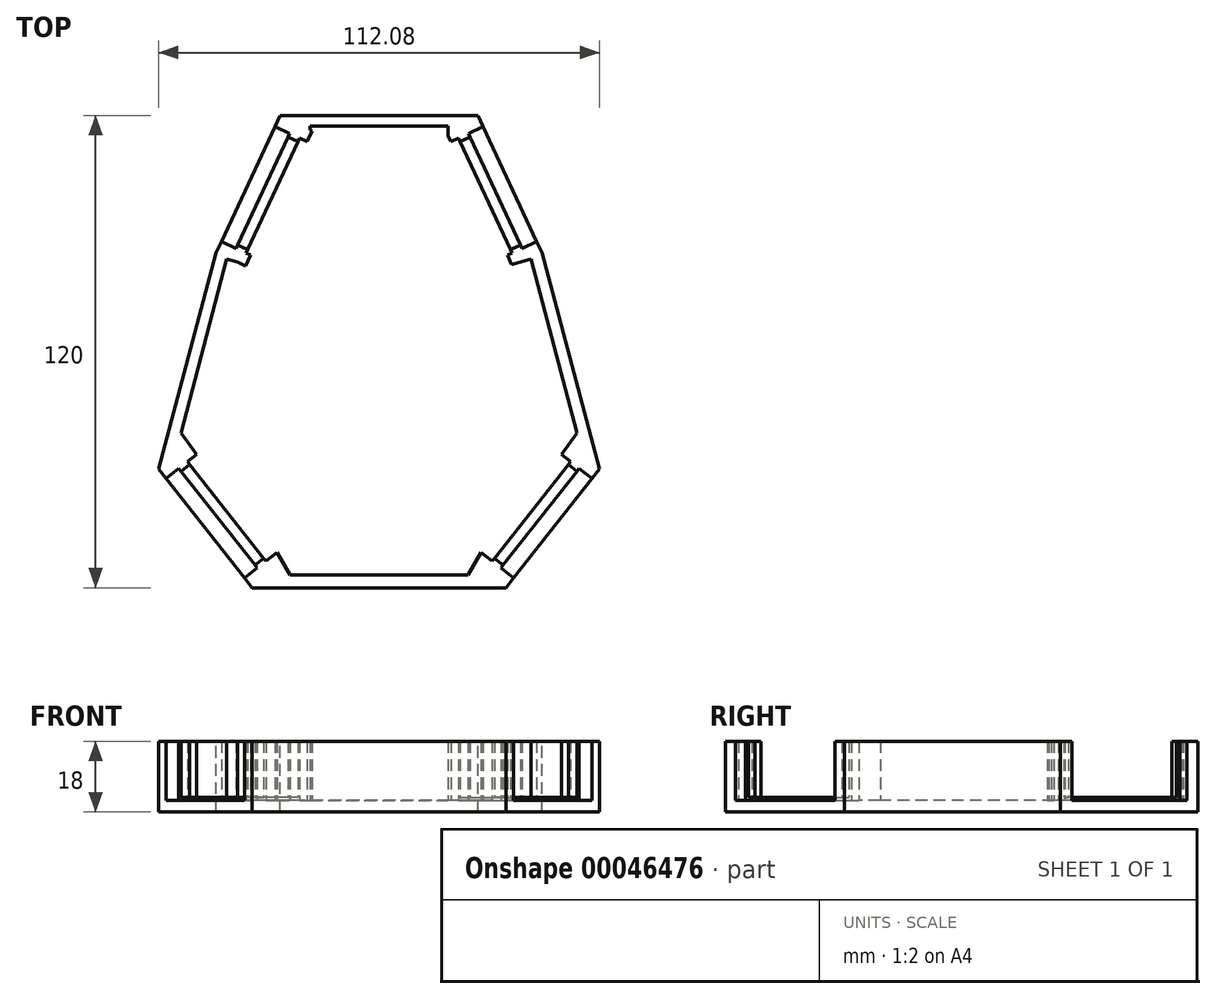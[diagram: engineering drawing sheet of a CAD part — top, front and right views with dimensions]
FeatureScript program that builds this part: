
annotation { "Feature Type Name" : "Feature", "Feature Type Description" : "" }
export const myFeature = defineFeature(function(context is Context, id is Id, definition is map)
    precondition{}
    {
        {
            assignVariable(context, id + "F0", {"name" : "Tooth", "anyValue" : .7});
        }
        {
            var Q0;
            Q0=qCreatedBy(makeId("Top.planeOp"),FACE);
            var sketch = newSketch(context, id + "F1", { "sketchPlane" : qUnion([Q0])});
            skLineSegment(sketch, "E0", {"start": v(0, 0) * mm, "end": v(-25.09, 0) * mm});
            skLineSegment(sketch, "E1", {"start": v(-25.09, 0) * mm, "end": v(-41.36, -34.9) * mm});
            skLineSegment(sketch, "E2", {"start": v(-41.36, -34.9) * mm, "end": v(-56.04, -89.77) * mm});
            skLineSegment(sketch, "E3", {"start": v(-56.04, -89.77) * mm, "end": v(-32.2, -120) * mm});
            skLineSegment(sketch, "E4", {"start": v(-32.2, -120) * mm, "end": v(0, -120) * mm});
            skLineSegment(sketch, "E5", {"start": v(0, -120) * mm, "end": v(0, 0) * mm, "construction": true});
            skLineSegment(sketch, "E6.MirrorCS", {"start": v(25.09, 0) * mm, "end": v(41.36, -34.9) * mm});
            skLineSegment(sketch, "E7.MirrorCS", {"start": v(41.36, -34.9) * mm, "end": v(56.04, -89.77) * mm});
            skLineSegment(sketch, "E8.MirrorCS", {"start": v(56.04, -89.77) * mm, "end": v(32.2, -120) * mm});
            skLineSegment(sketch, "E9.MirrorCS", {"start": v(32.2, -120) * mm, "end": v(0, -120) * mm});
            skLineSegment(sketch, "E10.MirrorCS", {"start": v(0, 0) * mm, "end": v(25.09, 0) * mm});
            skLineSegment(sketch, "E11.rect.bottom", {"start": v(18, -79.74) * mm, "end": v(-18, -79.74) * mm, "construction": true});
            skLineSegment(sketch, "E11.rect.top", {"start": v(18, -43.74) * mm, "end": v(-18, -43.74) * mm, "construction": true});
            skLineSegment(sketch, "E11.rect.left", {"start": v(18, -79.74) * mm, "end": v(18, -43.74) * mm, "construction": true});
            skLineSegment(sketch, "E11.rect.right", {"start": v(-18, -79.74) * mm, "end": v(-18, -43.74) * mm, "construction": true});
            skPoint(sketch, "E11.rect.middle", {"position": v(0, -61.74) * mm});
            skLineSegment(sketch, "E12.rect.bottom", {"start": v(19.3, -109.08) * mm, "end": v(-19.3, -109.08) * mm, "construction": true});
            skLineSegment(sketch, "E12.rect.top", {"start": v(19.3, -86.43) * mm, "end": v(-19.3, -86.43) * mm, "construction": true});
            skLineSegment(sketch, "E12.rect.left", {"start": v(19.3, -109.08) * mm, "end": v(19.3, -86.43) * mm, "construction": true});
            skLineSegment(sketch, "E12.rect.right", {"start": v(-19.3, -109.08) * mm, "end": v(-19.3, -86.43) * mm, "construction": true});
            skPoint(sketch, "E12.rect.middle", {"position": v(0, -97.76) * mm});
            skLineSegment(sketch, "E13", {"start": v(-33.22, -17.45) * mm, "end": v(-114.79, 20.59) * mm, "construction": true});
            skLineSegment(sketch, "E14", {"start": v(-114.79, 20.59) * mm, "end": v(-114.79, -160.6) * mm, "construction": true});
            skLineSegment(sketch, "E15", {"start": v(-114.79, -160.6) * mm, "end": v(-44.12, -104.88) * mm, "construction": true});
            skLineSegment(sketch, "E16.rect.bottom", {"start": v(14.48, -6.47) * mm, "end": v(-14.48, -6.47) * mm, "construction": true});
            skLineSegment(sketch, "E16.rect.top", {"start": v(14.48, -2.14) * mm, "end": v(-14.48, -2.14) * mm, "construction": true});
            skLineSegment(sketch, "E16.rect.left", {"start": v(14.48, -6.47) * mm, "end": v(14.48, -2.14) * mm, "construction": true});
            skLineSegment(sketch, "E16.rect.right", {"start": v(-14.48, -6.47) * mm, "end": v(-14.48, -2.14) * mm, "construction": true});
            skPoint(sketch, "E16.rect.middle", {"position": v(0, -4.3) * mm});
            skLineSegment(sketch, "E17.rect.bottom", {"start": v(9.65, -2.14) * mm, "end": v(-9.65, -2.14) * mm, "construction": true});
            skLineSegment(sketch, "E17.rect.top", {"start": v(9.65, 5.35) * mm, "end": v(-9.65, 5.35) * mm, "construction": true});
            skLineSegment(sketch, "E17.rect.left", {"start": v(9.65, -2.14) * mm, "end": v(9.65, 5.35) * mm, "construction": true});
            skLineSegment(sketch, "E17.rect.right", {"start": v(-9.65, -2.14) * mm, "end": v(-9.65, 5.35) * mm, "construction": true});
            skPoint(sketch, "E17.rect.middle", {"position": v(0, 1.6) * mm});
            skLineSegment(sketch, "E18.rect.bottom", {"start": v(10.77, -40.08) * mm, "end": v(-10.77, -40.08) * mm, "construction": true});
            skLineSegment(sketch, "E18.rect.top", {"start": v(10.77, -10) * mm, "end": v(-10.77, -10) * mm, "construction": true});
            skLineSegment(sketch, "E18.rect.left", {"start": v(10.77, -40.08) * mm, "end": v(10.77, -10) * mm, "construction": true});
            skLineSegment(sketch, "E18.rect.right", {"start": v(-10.77, -40.08) * mm, "end": v(-10.77, -10) * mm, "construction": true});
            skPoint(sketch, "E18.rect.middle", {"position": v(0, -25.04) * mm});
            skLineSegment(sketch, "E19.MirrorCS", {"start": v(114.79, -160.6) * mm, "end": v(44.12, -104.88) * mm, "construction": true});
            skLineSegment(sketch, "E20.MirrorCS", {"start": v(33.22, -17.45) * mm, "end": v(114.79, 20.59) * mm, "construction": true});
            skLineSegment(sketch, "E21.MirrorCS", {"start": v(114.79, 20.59) * mm, "end": v(114.79, -160.6) * mm, "construction": true});
            skLineSegment(sketch, "E22", {"start": v(-33.22, -17.45) * mm, "end": v(-28.24, -19.77) * mm, "construction": true});
            skLineSegment(sketch, "E23.rect.bottom", {"start": v(-20.43, -6.58) * mm, "end": v(-33.32, -34.23) * mm, "construction": true});
            skLineSegment(sketch, "E23.rect.top", {"start": v(-23.15, -5.32) * mm, "end": v(-36.04, -32.96) * mm, "construction": true});
            skLineSegment(sketch, "E23.rect.left", {"start": v(-20.43, -6.58) * mm, "end": v(-23.15, -5.32) * mm, "construction": true});
            skLineSegment(sketch, "E23.rect.right", {"start": v(-33.32, -34.23) * mm, "end": v(-36.04, -32.96) * mm, "construction": true});
            skPoint(sketch, "E23.rect.middle", {"position": v(-28.24, -19.77) * mm});
            skLineSegment(sketch, "E24", {"start": v(-44.12, -104.88) * mm, "end": v(-39.8, -101.48) * mm, "construction": true});
            skLineSegment(sketch, "E25.rect.bottom", {"start": v(-31.53, -114.38) * mm, "end": v(-50.42, -90.43) * mm, "construction": true});
            skLineSegment(sketch, "E25.rect.top", {"start": v(-29.18, -112.52) * mm, "end": v(-48.06, -88.57) * mm, "construction": true});
            skLineSegment(sketch, "E25.rect.left", {"start": v(-31.53, -114.38) * mm, "end": v(-29.18, -112.52) * mm, "construction": true});
            skLineSegment(sketch, "E25.rect.right", {"start": v(-50.42, -90.43) * mm, "end": v(-48.06, -88.57) * mm, "construction": true});
            skPoint(sketch, "E25.rect.middle", {"position": v(-39.8, -101.48) * mm});
            skSolve(sketch);
        }
        {
            var Q0;
            Q0=makeQuery(id+"F1.imprint","IMPRINT",FACE,{"disambiguationData":[TD([[makeQuery(id+"F1.imprint","IMPRINT",EDGE,{"derivedFrom":sQuery(id+"F1.wireOp",EDGE,"E0")}),1.0]])]});
            extrude(context, id + "F2", {"entities" : qUnion([Q0]), "oppositeDirection" : true, "depth" : 3 * mm});
        }
        {
            var Q0;
            Q0=makeQuery(id+"F2.opExtrude","CAP_FACE",FACE,{"disambiguationData":[OSD([sQuery(id+"F1.wireOp",EDGE,"E0"),sQuery(id+"F1.wireOp",EDGE,"E1"),sQuery(id+"F1.wireOp",EDGE,"E2"),sQuery(id+"F1.wireOp",EDGE,"E3"),sQuery(id+"F1.wireOp",EDGE,"E4"),sQuery(id+"F1.wireOp",EDGE,"E6.MirrorCS"),sQuery(id+"F1.wireOp",EDGE,"E7.MirrorCS"),sQuery(id+"F1.wireOp",EDGE,"E8.MirrorCS"),sQuery(id+"F1.wireOp",EDGE,"E9.MirrorCS"),sQuery(id+"F1.wireOp",EDGE,"E10.MirrorCS")])],"isStart":true});
            var sketch = newSketch(context, id + "F3", { "sketchPlane" : qUnion([Q0])});
            skPoint(sketch, "E26.0", {"position": v(-39.8, -101.48) * mm});
            skPoint(sketch, "E26.1", {"position": v(-28.24, -19.77) * mm});
            skLineSegment(sketch, "E27.rect.bottom", {"start": v(-20.57, -6.63) * mm, "end": v(-33.37, -34.1) * mm});
            skLineSegment(sketch, "E27.rect.top", {"start": v(-23.1, -5.45) * mm, "end": v(-35.9, -32.9) * mm});
            skLineSegment(sketch, "E27.rect.left", {"start": v(-20.57, -6.63) * mm, "end": v(-23.1, -5.45) * mm});
            skLineSegment(sketch, "E27.rect.right", {"start": v(-33.37, -34.1) * mm, "end": v(-35.9, -32.9) * mm});
            skLineSegment(sketch, "E28.rect.bottom", {"start": v(-31.52, -114.24) * mm, "end": v(-50.28, -90.45) * mm});
            skLineSegment(sketch, "E28.rect.top", {"start": v(-29.32, -112.5) * mm, "end": v(-48.08, -88.71) * mm});
            skLineSegment(sketch, "E28.rect.left", {"start": v(-31.52, -114.24) * mm, "end": v(-29.32, -112.5) * mm});
            skLineSegment(sketch, "E28.rect.right", {"start": v(-50.28, -90.45) * mm, "end": v(-48.08, -88.71) * mm});
            skLineSegment(sketch, "E29.MirrorCS", {"start": v(33.37, -34.1) * mm, "end": v(35.9, -32.9) * mm});
            skLineSegment(sketch, "E30.MirrorCS", {"start": v(20.57, -6.63) * mm, "end": v(23.1, -5.45) * mm});
            skPoint(sketch, "E31.MirrorP", {"position": v(28.24, -19.77) * mm});
            skLineSegment(sketch, "E32.MirrorCS", {"start": v(23.1, -5.45) * mm, "end": v(35.9, -32.9) * mm});
            skLineSegment(sketch, "E33.MirrorCS", {"start": v(20.57, -6.63) * mm, "end": v(33.37, -34.1) * mm});
            skLineSegment(sketch, "E34.MirrorCS", {"start": v(31.52, -114.24) * mm, "end": v(29.32, -112.5) * mm});
            skLineSegment(sketch, "E35.MirrorCS", {"start": v(31.52, -114.24) * mm, "end": v(50.28, -90.45) * mm});
            skLineSegment(sketch, "E36.MirrorCS", {"start": v(29.32, -112.5) * mm, "end": v(48.08, -88.71) * mm});
            skLineSegment(sketch, "E37.MirrorCS", {"start": v(50.28, -90.45) * mm, "end": v(48.08, -88.71) * mm});
            skSolve(sketch);
        }
        {
            var Q0;
            Q0 = qSketchRegion(id + "F3", true);
            extrude(context, id + "F4", {"entities" : qUnion([Q0]), "operationType" : NewBodyOperationType.ADD, "depth" : (getVariable(context, 'Tooth')) * mm});
        }
        {
            var Q0;
            Q0=makeQuery(id+"F1.imprint","IMPRINT",FACE,{"disambiguationData":[TD([[makeQuery(id+"F1.imprint","IMPRINT",EDGE,{"derivedFrom":sQuery(id+"F1.wireOp",EDGE,"E0")}),1.0]])]});
            var sketch = newSketch(context, id + "F5", { "sketchPlane" : qUnion([Q0])});
            skLineSegment(sketch, "E38.0", {"start": v(-20.57, -6.63) * mm, "end": v(-23.1, -5.45) * mm});
            skLineSegment(sketch, "E38.1", {"start": v(-33.37, -34.1) * mm, "end": v(-35.9, -32.9) * mm});
            skLineSegment(sketch, "E38.2", {"start": v(-50.28, -90.45) * mm, "end": v(-48.08, -88.71) * mm});
            skLineSegment(sketch, "E38.3", {"start": v(-31.52, -114.24) * mm, "end": v(-29.32, -112.5) * mm});
            skLineSegment(sketch, "E39", {"start": v(-25.88, -111) * mm, "end": v(-22.63, -116.77) * mm});
            skLineSegment(sketch, "E40", {"start": v(-22.63, -116.77) * mm, "end": v(0, -116.77) * mm});
            skLineSegment(sketch, "E41.0", {"start": v(-32.2, -120) * mm, "end": v(0, -120) * mm});
            skLineSegment(sketch, "E41.2", {"start": v(-41.36, -34.9) * mm, "end": v(-56.04, -89.77) * mm});
            skLineSegment(sketch, "E42", {"start": v(-32.6, -35.5) * mm, "end": v(-33.7, -37.85) * mm});
            skLineSegment(sketch, "E43", {"start": v(-33.7, -37.85) * mm, "end": v(-38.68, -36.54) * mm});
            skLineSegment(sketch, "E44", {"start": v(-38.68, -36.54) * mm, "end": v(-50.24, -80.68) * mm});
            skLineSegment(sketch, "E45", {"start": v(-50.24, -80.68) * mm, "end": v(-46.34, -86.14) * mm});
            skLineSegment(sketch, "E46", {"start": v(-54.08, -92.24) * mm, "end": v(-50.87, -89.7) * mm});
            skLineSegment(sketch, "E47", {"start": v(-50.87, -89.7) * mm, "end": v(-50.28, -90.45) * mm});
            skLineSegment(sketch, "E48", {"start": v(-48.08, -88.71) * mm, "end": v(-48.67, -87.97) * mm});
            skLineSegment(sketch, "E49", {"start": v(-48.67, -87.97) * mm, "end": v(-46.34, -86.14) * mm});
            skLineSegment(sketch, "E50", {"start": v(-29.32, -112.5) * mm, "end": v(-28.73, -113.25) * mm});
            skLineSegment(sketch, "E51", {"start": v(-28.73, -113.25) * mm, "end": v(-25.88, -111) * mm});
            skLineSegment(sketch, "E52", {"start": v(-31.52, -114.24) * mm, "end": v(-30.93, -114.99) * mm});
            skLineSegment(sketch, "E53", {"start": v(-30.93, -114.99) * mm, "end": v(-34.15, -117.53) * mm});
            skLineSegment(sketch, "E54", {"start": v(-34.15, -117.53) * mm, "end": v(-32.2, -120) * mm});
            skLineSegment(sketch, "E55", {"start": v(-52.48, -90.97) * mm, "end": v(-32.54, -116.26) * mm, "construction": true});
            skLineSegment(sketch, "E56", {"start": v(-40.03, -32.04) * mm, "end": v(-41.36, -34.9) * mm});
            skLineSegment(sketch, "E57", {"start": v(-33.37, -34.1) * mm, "end": v(-33.77, -34.95) * mm});
            skLineSegment(sketch, "E58", {"start": v(-33.77, -34.95) * mm, "end": v(-32.6, -35.5) * mm});
            skLineSegment(sketch, "E59", {"start": v(-35.9, -32.9) * mm, "end": v(-36.31, -33.77) * mm});
            skLineSegment(sketch, "E60", {"start": v(-36.31, -33.77) * mm, "end": v(-40.03, -32.04) * mm});
            skLineSegment(sketch, "E61", {"start": v(-20.57, -6.63) * mm, "end": v(-20.16, -5.77) * mm});
            skLineSegment(sketch, "E62", {"start": v(-20.16, -5.77) * mm, "end": v(-18.23, -6.67) * mm});
            skLineSegment(sketch, "E63", {"start": v(-18.23, -6.67) * mm, "end": v(-17.56, -5.21) * mm});
            skLineSegment(sketch, "E64", {"start": v(-17.56, -5.21) * mm, "end": v(-17.56, -2.74) * mm});
            skLineSegment(sketch, "E65", {"start": v(-17.56, -2.74) * mm, "end": v(0, -2.74) * mm});
            skLineSegment(sketch, "E66", {"start": v(-23.1, -5.45) * mm, "end": v(-22.7, -4.59) * mm});
            skLineSegment(sketch, "E67", {"start": v(-22.7, -4.59) * mm, "end": v(-26.42, -2.85) * mm});
            skLineSegment(sketch, "E68", {"start": v(-26.42, -2.85) * mm, "end": v(-25.09, 0) * mm});
            skLineSegment(sketch, "E69", {"start": v(-25.09, 0) * mm, "end": v(0, 0) * mm});
            skPoint(sketch, "E70.0", {"position": v(-25.09, 0) * mm});
            skLineSegment(sketch, "E71", {"start": v(-24.56, -3.72) * mm, "end": v(-38.17, -32.9) * mm, "construction": true});
            skLineSegment(sketch, "E72", {"start": v(-54.08, -92.24) * mm, "end": v(-56.04, -89.77) * mm});
            skLineSegment(sketch, "E73.MirrorCS", {"start": v(20.57, -6.63) * mm, "end": v(20.16, -5.77) * mm});
            skLineSegment(sketch, "E74.MirrorCS", {"start": v(31.52, -114.24) * mm, "end": v(30.93, -114.99) * mm});
            skLineSegment(sketch, "E75.MirrorCS", {"start": v(20.16, -5.77) * mm, "end": v(18.23, -6.67) * mm});
            skLineSegment(sketch, "E76.MirrorCS", {"start": v(29.32, -112.5) * mm, "end": v(28.73, -113.25) * mm});
            skLineSegment(sketch, "E77.MirrorCS", {"start": v(35.9, -32.9) * mm, "end": v(36.31, -33.77) * mm});
            skLineSegment(sketch, "E78.MirrorCS", {"start": v(33.37, -34.1) * mm, "end": v(35.9, -32.9) * mm});
            skLineSegment(sketch, "E79.MirrorCS", {"start": v(20.57, -6.63) * mm, "end": v(23.1, -5.45) * mm});
            skLineSegment(sketch, "E80.MirrorCS", {"start": v(33.37, -34.1) * mm, "end": v(33.77, -34.95) * mm});
            skLineSegment(sketch, "E81.MirrorCS", {"start": v(50.28, -90.45) * mm, "end": v(48.08, -88.71) * mm});
            skLineSegment(sketch, "E82.MirrorCS", {"start": v(48.08, -88.71) * mm, "end": v(48.67, -87.97) * mm});
            skLineSegment(sketch, "E83.MirrorCS", {"start": v(23.1, -5.45) * mm, "end": v(22.7, -4.59) * mm});
            skLineSegment(sketch, "E84.MirrorCS", {"start": v(31.52, -114.24) * mm, "end": v(29.32, -112.5) * mm});
            skLineSegment(sketch, "E85.MirrorCS", {"start": v(50.87, -89.7) * mm, "end": v(50.28, -90.45) * mm});
            skLineSegment(sketch, "E86.MirrorCS", {"start": v(26.42, -2.85) * mm, "end": v(25.09, 0) * mm});
            skLineSegment(sketch, "E87.MirrorCS", {"start": v(36.31, -33.77) * mm, "end": v(40.03, -32.04) * mm});
            skLineSegment(sketch, "E88.MirrorCS", {"start": v(40.03, -32.04) * mm, "end": v(41.36, -34.9) * mm});
            skLineSegment(sketch, "E89.MirrorCS", {"start": v(50.24, -80.68) * mm, "end": v(46.34, -86.14) * mm});
            skLineSegment(sketch, "E90.MirrorCS", {"start": v(54.08, -92.24) * mm, "end": v(50.87, -89.7) * mm});
            skLineSegment(sketch, "E91.MirrorCS", {"start": v(33.77, -34.95) * mm, "end": v(32.6, -35.5) * mm});
            skLineSegment(sketch, "E92.MirrorCS", {"start": v(33.7, -37.85) * mm, "end": v(38.68, -36.54) * mm});
            skLineSegment(sketch, "E93.MirrorCS", {"start": v(30.93, -114.99) * mm, "end": v(34.15, -117.53) * mm});
            skLineSegment(sketch, "E94.MirrorCS", {"start": v(17.56, -5.21) * mm, "end": v(17.56, -2.74) * mm});
            skLineSegment(sketch, "E95.MirrorCS", {"start": v(54.08, -92.24) * mm, "end": v(56.04, -89.77) * mm});
            skLineSegment(sketch, "E96.MirrorCS", {"start": v(32.6, -35.5) * mm, "end": v(33.7, -37.85) * mm});
            skLineSegment(sketch, "E97.MirrorCS", {"start": v(18.23, -6.67) * mm, "end": v(17.56, -5.21) * mm});
            skLineSegment(sketch, "E98.MirrorCS", {"start": v(34.15, -117.53) * mm, "end": v(32.2, -120) * mm});
            skLineSegment(sketch, "E99.MirrorCS", {"start": v(28.73, -113.25) * mm, "end": v(25.88, -111) * mm});
            skLineSegment(sketch, "E100.MirrorCS", {"start": v(48.67, -87.97) * mm, "end": v(46.34, -86.14) * mm});
            skLineSegment(sketch, "E101.MirrorCS", {"start": v(22.7, -4.59) * mm, "end": v(26.42, -2.85) * mm});
            skLineSegment(sketch, "E102.MirrorCS", {"start": v(25.88, -111) * mm, "end": v(22.63, -116.77) * mm});
            skLineSegment(sketch, "E103.MirrorCS", {"start": v(17.56, -2.74) * mm, "end": v(0, -2.74) * mm});
            skLineSegment(sketch, "E104.MirrorCS", {"start": v(25.09, 0) * mm, "end": v(0, 0) * mm});
            skLineSegment(sketch, "E105.MirrorCS", {"start": v(38.68, -36.54) * mm, "end": v(50.24, -80.68) * mm});
            skPoint(sketch, "E106.MirrorP", {"position": v(25.09, 0) * mm});
            skLineSegment(sketch, "E107.MirrorCS", {"start": v(32.2, -120) * mm, "end": v(0, -120) * mm});
            skLineSegment(sketch, "E108.MirrorCS", {"start": v(52.48, -90.97) * mm, "end": v(32.54, -116.26) * mm, "construction": true});
            skLineSegment(sketch, "E109.MirrorCS", {"start": v(24.56, -3.72) * mm, "end": v(38.17, -32.9) * mm, "construction": true});
            skLineSegment(sketch, "E110.MirrorCS", {"start": v(41.36, -34.9) * mm, "end": v(56.04, -89.77) * mm});
            skLineSegment(sketch, "E111.MirrorCS", {"start": v(22.63, -116.77) * mm, "end": v(0, -116.77) * mm});
            skSolve(sketch);
        }
        {
            var Q0;
            Q0 = qSketchRegion(id + "F5", true);
            extrude(context, id + "F6", {"entities" : qUnion([Q0]), "operationType" : NewBodyOperationType.ADD, "depth" : 15 * mm});
        }
        {
            var Q0;
            Q0 = qSketchRegion(id + "F3", true);
            extrude(context, id + "F7", {"entities" : qUnion([Q0]), "depth" : getVariable(context, 'Tooth') * mm});
        }
        {
            var Q0;
            Q0=makeQuery(id+"F7.opExtrude","SWEPT_BODY",BODY,{"disambiguationData":[OSD([sQuery(id+"F3.wireOp",EDGE,"E28.rect.bottom"),sQuery(id+"F3.wireOp",EDGE,"E28.rect.top"),sQuery(id+"F3.wireOp",EDGE,"E28.rect.left"),sQuery(id+"F3.wireOp",EDGE,"E28.rect.right")])]});
            var Q1;
            Q1=makeQuery(id+"F7.opExtrude","SWEPT_BODY",BODY,{"disambiguationData":[OSD([sQuery(id+"F3.wireOp",EDGE,"E29.MirrorCS"),sQuery(id+"F3.wireOp",EDGE,"E30.MirrorCS"),sQuery(id+"F3.wireOp",EDGE,"E32.MirrorCS"),sQuery(id+"F3.wireOp",EDGE,"E33.MirrorCS")])]});
            var Q2;
            Q2=makeQuery(id+"F7.opExtrude","SWEPT_BODY",BODY,{"disambiguationData":[OSD([sQuery(id+"F3.wireOp",EDGE,"E34.MirrorCS"),sQuery(id+"F3.wireOp",EDGE,"E35.MirrorCS"),sQuery(id+"F3.wireOp",EDGE,"E36.MirrorCS"),sQuery(id+"F3.wireOp",EDGE,"E37.MirrorCS")])]});
            deleteBodies(context, id + "F8", {"entities" : qUnion([Q0, Q1, Q2])});
        }
        {
            var Q0;
            Q0=qCreatedBy(makeId("Top.planeOp"),FACE);
            var sketch = newSketch(context, id + "F9", { "sketchPlane" : qUnion([Q0])});
            skLineSegment(sketch, "E112.0", {"start": v(-35.9, -32.9) * mm, "end": v(-36.31, -33.77) * mm});
            skLineSegment(sketch, "E112.1", {"start": v(-36.31, -33.77) * mm, "end": v(-40.03, -32.04) * mm});
            skLineSegment(sketch, "E112.2", {"start": v(-33.77, -34.95) * mm, "end": v(-32.6, -35.5) * mm});
            skLineSegment(sketch, "E112.3", {"start": v(-33.37, -34.1) * mm, "end": v(-33.77, -34.95) * mm});
            skLineSegment(sketch, "E112.4", {"start": v(-33.37, -34.1) * mm, "end": v(-35.9, -32.9) * mm});
            skLineSegment(sketch, "E112.5", {"start": v(-20.16, -5.77) * mm, "end": v(-18.23, -6.67) * mm});
            skLineSegment(sketch, "E112.6", {"start": v(-20.57, -6.63) * mm, "end": v(-20.16, -5.77) * mm});
            skLineSegment(sketch, "E112.7", {"start": v(-20.57, -6.63) * mm, "end": v(-23.1, -5.45) * mm});
            skLineSegment(sketch, "E112.8", {"start": v(-23.1, -5.45) * mm, "end": v(-22.7, -4.59) * mm});
            skLineSegment(sketch, "E112.9", {"start": v(-22.7, -4.59) * mm, "end": v(-26.42, -2.85) * mm});
            skLineSegment(sketch, "E113", {"start": v(-26.42, -2.85) * mm, "end": v(-25.15, -0.14) * mm});
            skLineSegment(sketch, "E114", {"start": v(-25.15, -0.14) * mm, "end": v(-16.97, -3.95) * mm});
            skLineSegment(sketch, "E115", {"start": v(-16.97, -3.95) * mm, "end": v(-18.23, -6.67) * mm});
            skLineSegment(sketch, "E116", {"start": v(-32.6, -35.5) * mm, "end": v(-33.87, -38.22) * mm});
            skLineSegment(sketch, "E117", {"start": v(-33.87, -38.22) * mm, "end": v(-41.3, -34.76) * mm});
            skLineSegment(sketch, "E118", {"start": v(-41.3, -34.76) * mm, "end": v(-40.03, -32.04) * mm});
            skSolve(sketch);
        }
        {
            var Q0;
            Q0 = qSketchRegion(id + "F9", true);
            extrude(context, id + "F10", {"entities" : qUnion([Q0]), "operationType" : NewBodyOperationType.ADD, "depth" : 15 * mm});
        }
        {
            var Q0;
            Q0=qCreatedBy(makeId("Top.planeOp"),FACE);
            var sketch = newSketch(context, id + "F11", { "sketchPlane" : qUnion([Q0])});
            skPoint(sketch, "E119.0", {"position": v(-25.15, -0.14) * mm});
            skPoint(sketch, "E119.1", {"position": v(-16.97, -3.95) * mm});
            skPoint(sketch, "E119.2", {"position": v(-33.87, -38.22) * mm});
            skLineSegment(sketch, "E120", {"start": v(-33.87, -38.22) * mm, "end": v(-16.97, -3.95) * mm});
            skLineSegment(sketch, "E121", {"start": v(-16.97, -3.95) * mm, "end": v(-25.15, -0.14) * mm});
            skPoint(sketch, "E122.0", {"position": v(-41.3, -34.76) * mm});
            skLineSegment(sketch, "E123", {"start": v(-41.3, -34.76) * mm, "end": v(-33.87, -38.22) * mm});
            skLineSegment(sketch, "E124", {"start": v(-41.3, -34.76) * mm, "end": v(-25.15, -0.14) * mm});
            skSolve(sketch);
        }
        {
            var Q0;
            Q0 = qSketchRegion(id + "F11", true);
            extrude(context, id + "F12", {"entities" : qUnion([Q0]), "operationType" : NewBodyOperationType.ADD, "oppositeDirection" : true, "depth" : 3 * mm});
        }
    });
